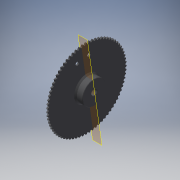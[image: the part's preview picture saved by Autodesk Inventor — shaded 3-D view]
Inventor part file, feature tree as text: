
AUTODESK INVENTOR PART (.ipt)
format: ipt  version: 2018 (Build 220112000, 112)  size: 899,072 bytes
history: native  units: mm
features: sketch x4, revolve x1, extrude x1, hole x1, other x1
ambient origin geometry x8: Origin, YZ Plane, XZ Plane, XY Plane, X Axis, Y Axis, Z Axis, Center Point
bodies: Solid1 (feature_tree), body_XY (feature_tree), body_YZ (feature_tree), body_ZX (feature_tree), body_X (feature_tree), body_Y (feature_tree), body_Z (feature_tree), body_Center (feature_tree)
feature tree (8):
  revolve  "Revolution1"  [1 undecoded]
  extrude  "Extrusion1"  Depth=10.0mm
  sketch  "スケッチ3"
  hole  "穴1"  [1 undecoded]
  sketch  "スケッチ4"
  other  "作業平面4"
  sketch  "Sketch_5"  dims[d0=360.0deg d1=4.7mm d2=0.0mm]
  sketch  "Sketch_7"  dims[d3=0.0mm d4=164.0mm d5=160.412mm d6=90.0deg d7=10.0mm d8=6.0mm d9=4.0mm d10=2.0mm d11=90.0deg d12=8.0mm d13=20.594885mm d14=90.0deg]
note: 2 required parameter values undecoded (feature->parameter linkage not recoverable at this tier; creation-order binding heuristic only, values carry confidence <= 0.55)